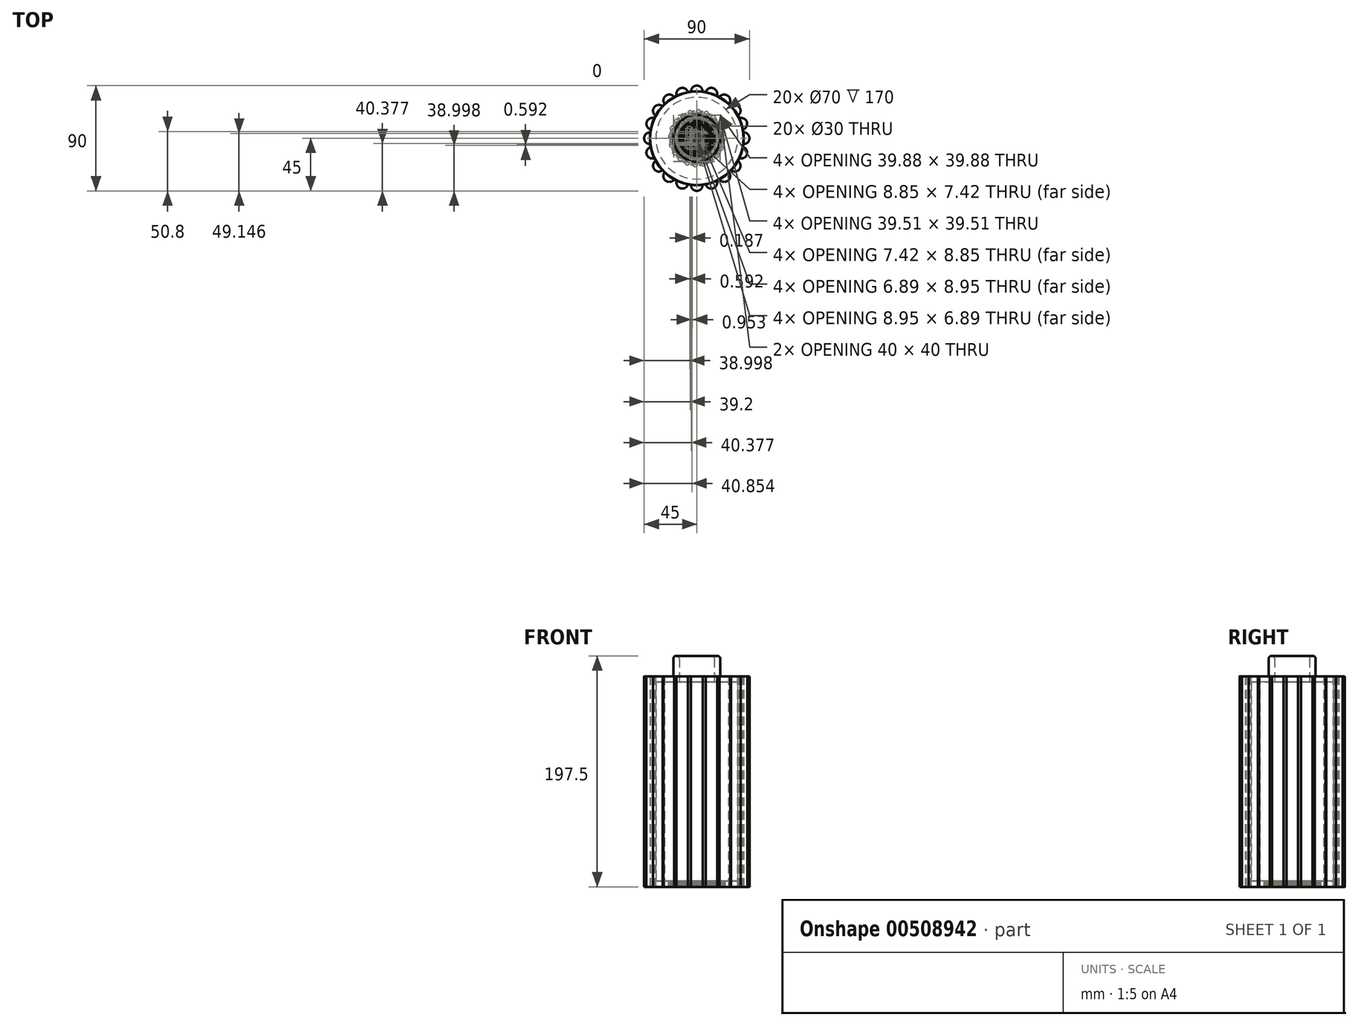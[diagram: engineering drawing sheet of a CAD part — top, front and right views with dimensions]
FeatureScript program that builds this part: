
annotation { "Feature Type Name" : "Feature", "Feature Type Description" : "" }
export const myFeature = defineFeature(function(context is Context, id is Id, definition is map)
    precondition{}
    {
        {
            var Q0;
            Q0=qCreatedBy(makeId("Top.planeOp"),FACE);
            var sketch = newSketch(context, id + "F0", { "sketchPlane" : qUnion([Q0])});
            skCircle(sketch, "E0", {"center": v(0, 0) * mm, "radius": 40 * mm});
            skSolve(sketch);
        }
        {
            var Q0;
            Q0 = qSketchRegion(id + "F0", true);
            extrude(context, id + "F1", {"entities" : qUnion([Q0]), "depth" : 180 * mm});
        }
        {
            var Q0;
            Q0=makeQuery(id+"F1.opExtrude","CAP_FACE",FACE,{"disambiguationData":[OSD([sQuery(id+"F0.wireOp",EDGE,"E0")])],"isStart":false});
            var sketch = newSketch(context, id + "F2", { "sketchPlane" : qUnion([Q0])});
            skCircle(sketch, "E1", {"center": v(0, 0) * mm, "radius": 20 * mm});
            skSolve(sketch);
        }
        {
            var Q0;
            Q0 = qSketchRegion(id + "F2", true);
            extrude(context, id + "F3", {"entities" : qUnion([Q0]), "operationType" : NewBodyOperationType.ADD, "depth" : 20 * mm});
        }
        {
            var Q0;
            Q0=makeQuery(id+"F3.opExtrude","CAP_FACE",FACE,{"disambiguationData":[OSD([sQuery(id+"F2.wireOp",EDGE,"E1")])],"isStart":false});
            shell(context, id + "F4", {"entities" : qUnion([Q0]), "thickness" : 5 * mm});
        }
        {
            var Q0;
            {var subQ0=sQuery(id+"F2.wireOp",EDGE,"E1");Q0=makeQuery(id+"F4.opShell","OFFSET_EDGE",EDGE,{"disambiguationData":[OSD([subQ0]),TDD([makeQuery(id+"F3.opExtrude","CAP_EDGE",EDGE,{"disambiguationData":[OSD([subQ0])],"isStart":false})])]});}
            fillet(context, id + "F5", {"entities" : qUnion([Q0]), "radius" : 5 * mm, "tangentPropagation" : true, "allowEdgeOverflow" : false});
        }
        {
            var Q0;
            {var subQ0=sQuery(id+"F2.wireOp",EDGE,"E1");Q0=makeQuery(id+"F5.opFillet","BLEND_EDGE",EDGE,{"blendedFrom":[makeQuery(id+"F4.opShell","OFFSET_EDGE",EDGE,{"disambiguationData":[OSD([subQ0]),TDD([makeQuery(id+"F3.opExtrude","CAP_EDGE",EDGE,{"disambiguationData":[OSD([subQ0])],"isStart":false})])]}),makeQuery(id+"F3.opExtrude","SWEPT_FACE",FACE,{"disambiguationData":[OSD([subQ0])]})],"blendedInto":[makeQuery(id+"F3.opExtrude","SWEPT_FACE",FACE,{"disambiguationData":[OSD([subQ0])]})]});}
            var Q1;
            Q1=makeQuery(id+"F5.opFillet","BLEND_FACE",FACE,{"disambiguationData":[OSD([sQuery(id+"F2.wireOp",EDGE,"E1")])]});
            fillet(context, id + "F6", {"entities" : qUnion([Q0, Q1]), "radius" : 2.5 * mm, "tangentPropagation" : true, "allowEdgeOverflow" : false});
        }
        {
            var Q0;
            Q0=makeQuery(id+"F1.opExtrude","CAP_FACE",FACE,{"disambiguationData":[OSD([sQuery(id+"F0.wireOp",EDGE,"E0")])],"isStart":true});
            var sketch = newSketch(context, id + "F7", { "sketchPlane" : qUnion([Q0])});
            skText(sketch, "E2", { "text": "Savage", "fontName": "OpenSans-BoldItalic.ttf"});
            const initialGuessF7  = {"E2": [-0.01785, -0.00384, 1, 0, 0.00918]};
            skSetInitialGuess(sketch, initialGuessF7);
            skSolve(sketch);
        }
        {
            var Q0;
            Q0 = qSketchRegion(id + "F7", true);
            extrude(context, id + "F8", {"entities" : qUnion([Q0]), "operationType" : NewBodyOperationType.REMOVE, "oppositeDirection" : true, "depth" : 5 * mm});
        }
        {
            var Q0;
            Q0=makeQuery(id+"F1.opExtrude","CAP_FACE",FACE,{"disambiguationData":[OSD([sQuery(id+"F0.wireOp",EDGE,"E0")])],"isStart":false});
            var sketch = newSketch(context, id + "F9", { "sketchPlane" : qUnion([Q0])});
            skCircle(sketch, "E3", {"center": v(0, -40) * mm, "radius": 5 * mm});
            skSolve(sketch);
        }
        {
            var Q0;
            {var subQ0=sQuery(id+"F9.wireOp",EDGE,"E3");var subQ1=makeQuery(id+"F1.opExtrude","CAP_EDGE",EDGE,{"disambiguationData":[OSD([sQuery(id+"F0.wireOp",EDGE,"E0")])],"isStart":false});var subQ2=makeQuery(id+"F9.imprint","INTERSECT",VERTEX,{"disambiguationData":[OD(0.0)],"derivedFrom":[subQ1,subQ0]});Q0=makeQuery(id+"F9.imprint","IMPRINT",FACE,{"disambiguationData":[TD([[makeQuery(id+"F9.imprint","IMPRINT",EDGE,{"disambiguationData":[TD([[subQ2,-1.0]])],"derivedFrom":subQ0}),1.0]])]});}
            extrude(context, id + "F10", {"entities" : qUnion([Q0]), "operationType" : NewBodyOperationType.ADD, "oppositeDirection" : true, "depth" : 180 * mm, "offsetDistance" : 25 * mm});
        }
        {
            var Q0;
            Q0=makeQuery(id+"F8.boolean.opBoolean","SPLIT",BODY,{"disambiguationData":[OD(0.0)],"derivedFrom":makeQuery(id+"F1.opExtrude","SWEPT_BODY",BODY,{"disambiguationData":[OSD([sQuery(id+"F0.wireOp",EDGE,"E0")])]})});
            var Q1;
            Q1=makeQuery(id+"F1.opExtrude","SWEPT_FACE",FACE,{"disambiguationData":[OSD([sQuery(id+"F0.wireOp",EDGE,"E0")])]});
            circularPattern(context, id + "F11", {"entities" : qUnion([Q0]), "axis" : qUnion([Q1]), "angle" : 360 * degree, "instanceCount" : 20, "equalSpace" : true});
        }
    });
